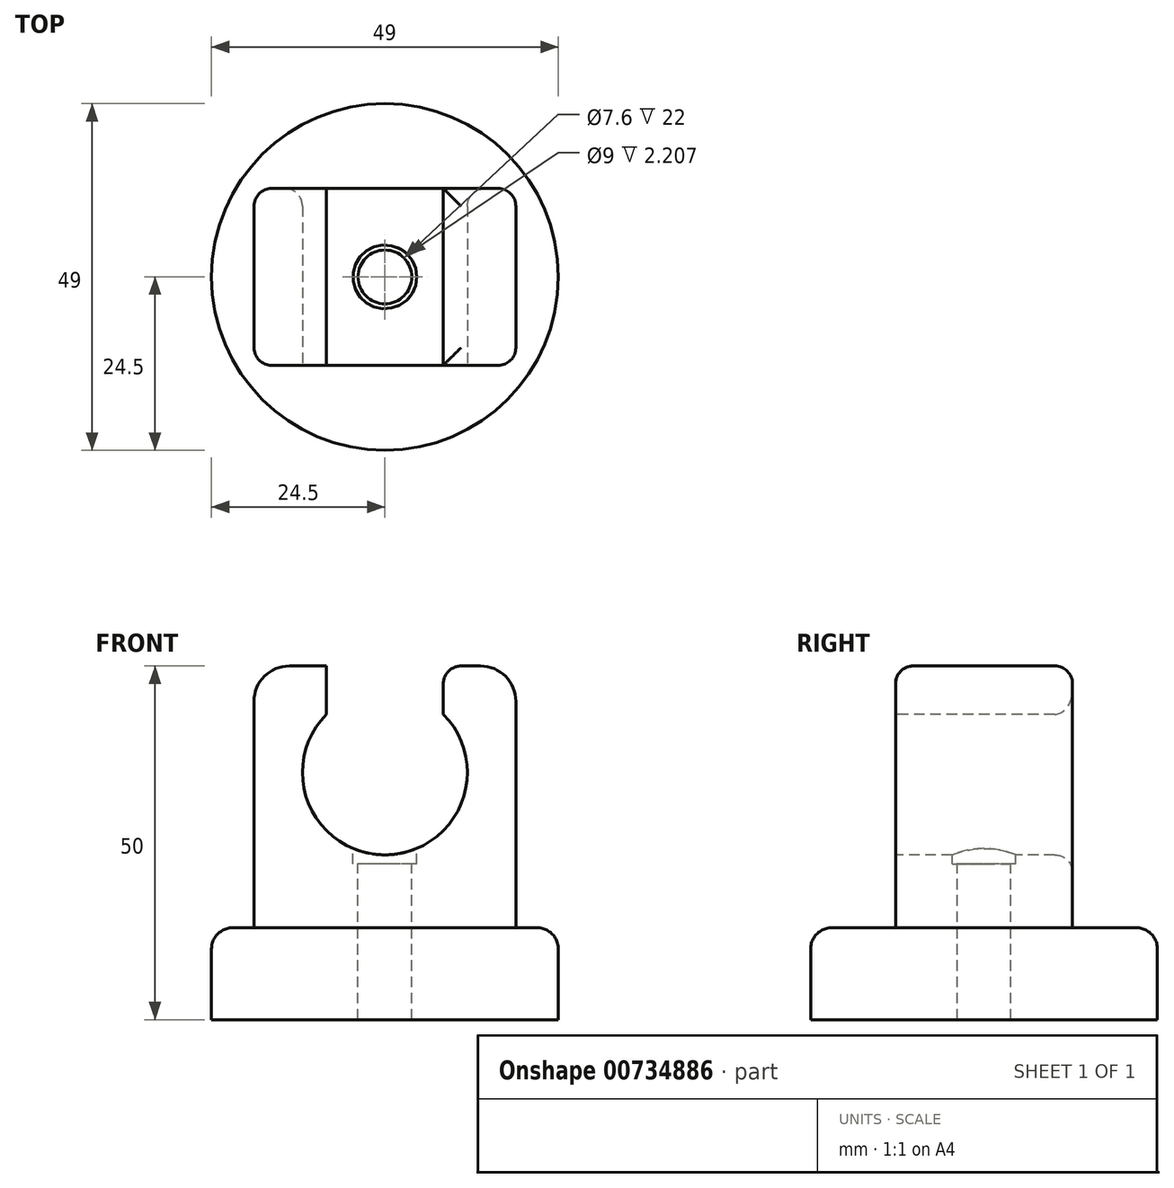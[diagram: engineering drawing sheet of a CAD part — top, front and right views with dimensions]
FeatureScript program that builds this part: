
annotation { "Feature Type Name" : "Feature", "Feature Type Description" : "" }
export const myFeature = defineFeature(function(context is Context, id is Id, definition is map)
    precondition{}
    {
        {
            var Q0;
            Q0=qCreatedBy(makeId("Top.planeOp"),FACE);
            var sketch = newSketch(context, id + "F0", { "sketchPlane" : qUnion([Q0])});
            skCircle(sketch, "E0", {"center": v(0, 0) * mm, "radius": 24.5 * mm});
            skSolve(sketch);
        }
        {
            var Q0;
            Q0=makeQuery(id+"F0.imprint","IMPRINT",FACE,{"disambiguationData":[TD([[makeQuery(id+"F0.imprint","IMPRINT",EDGE,{"derivedFrom":sQuery(id+"F0.wireOp",EDGE,"E0")}),1.0]])]});
            extrude(context, id + "F1", {"entities" : qUnion([Q0]), "depth" : 13 * mm, "offsetDistance" : 25.4 * mm});
        }
        {
            var Q0;
            Q0=makeQuery(id+"F1.opExtrude","CAP_FACE",FACE,{"disambiguationData":[OSD([sQuery(id+"F0.wireOp",EDGE,"E0")])],"isStart":false});
            var sketch = newSketch(context, id + "F2", { "sketchPlane" : qUnion([Q0])});
            skLineSegment(sketch, "E1.bottom", {"start": v(18.5, 12.5) * mm, "end": v(-18.5, 12.5) * mm});
            skLineSegment(sketch, "E1.top", {"start": v(18.5, -12.5) * mm, "end": v(-18.5, -12.5) * mm});
            skLineSegment(sketch, "E1.left", {"start": v(18.5, 12.5) * mm, "end": v(18.5, -12.5) * mm});
            skLineSegment(sketch, "E1.right", {"start": v(-18.5, 12.5) * mm, "end": v(-18.5, -12.5) * mm});
            skPoint(sketch, "E1.middle", {"position": v(0, 0) * mm});
            skSolve(sketch);
        }
        {
            var Q0;
            Q0=makeQuery(id+"F2.imprint","IMPRINT",FACE,{"disambiguationData":[TD([[makeQuery(id+"F2.imprint","IMPRINT",EDGE,{"derivedFrom":sQuery(id+"F2.wireOp",EDGE,"E1.bottom")}),1.0]])]});
            extrude(context, id + "F3", {"entities" : qUnion([Q0]), "operationType" : NewBodyOperationType.ADD, "depth" : 37 * mm, "offsetDistance" : 25.4 * mm});
        }
        {
            var Q0;
            Q0=makeQuery(id+"F1.opExtrude","CAP_EDGE",EDGE,{"disambiguationData":[OSD([sQuery(id+"F0.wireOp",EDGE,"E0")])],"isStart":false});
            fillet(context, id + "F4", {"entities" : qUnion([Q0]), "radius" : 3 * mm, "tangentPropagation" : true, "allowEdgeOverflow" : false});
        }
        {
            var Q0;
            Q0=makeQuery(id+"F3.opExtrude","CAP_FACE",FACE,{"disambiguationData":[OSD([sQuery(id+"F2.wireOp",EDGE,"E1.bottom"),sQuery(id+"F2.wireOp",EDGE,"E1.top"),sQuery(id+"F2.wireOp",EDGE,"E1.left"),sQuery(id+"F2.wireOp",EDGE,"E1.right")])],"isStart":false});
            var sketch = newSketch(context, id + "F5", { "sketchPlane" : qUnion([Q0])});
            skCircle(sketch, "E2", {"center": v(0, 0) * mm, "radius": 3.8 * mm});
            skSolve(sketch);
        }
        {
            var Q0;
            Q0=makeQuery(id+"F5.imprint","IMPRINT",FACE,{"disambiguationData":[TD([[makeQuery(id+"F5.imprint","IMPRINT",EDGE,{"derivedFrom":sQuery(id+"F5.wireOp",EDGE,"E2")}),1.0]])]});
            extrude(context, id + "F6", {"entities" : qUnion([Q0]), "operationType" : NewBodyOperationType.REMOVE, "oppositeDirection" : true, "depth" : 60 * mm, "offsetDistance" : 25.4 * mm});
        }
        {
            var Q0;
            Q0=makeQuery(id+"F3.opExtrude","SWEPT_FACE",FACE,{"disambiguationData":[OSD([sQuery(id+"F2.wireOp",EDGE,"E1.top")])]});
            var sketch = newSketch(context, id + "F7", { "sketchPlane" : qUnion([Q0])});
            skCircle(sketch, "E3", {"center": v(0, 34.95) * mm, "radius": 11.65 * mm});
            skSolve(sketch);
        }
        {
            var Q0;
            Q0=makeQuery(id+"F7.imprint","IMPRINT",FACE,{"disambiguationData":[TD([[makeQuery(id+"F7.imprint","IMPRINT",EDGE,{"derivedFrom":sQuery(id+"F7.wireOp",EDGE,"E3")}),1.0]])]});
            extrude(context, id + "F8", {"entities" : qUnion([Q0]), "operationType" : NewBodyOperationType.REMOVE, "oppositeDirection" : true, "depth" : 40 * mm, "offsetDistance" : 25.4 * mm});
        }
        {
            var Q0;
            Q0=makeQuery(id+"F3.opExtrude","CAP_FACE",FACE,{"disambiguationData":[OSD([sQuery(id+"F2.wireOp",EDGE,"E1.bottom"),sQuery(id+"F2.wireOp",EDGE,"E1.top"),sQuery(id+"F2.wireOp",EDGE,"E1.left"),sQuery(id+"F2.wireOp",EDGE,"E1.right")])],"isStart":false});
            var sketch = newSketch(context, id + "F9", { "sketchPlane" : qUnion([Q0])});
            skLineSegment(sketch, "E4.bottom", {"start": v(8.25, 12.5) * mm, "end": v(-8.25, 12.5) * mm});
            skLineSegment(sketch, "E4.top", {"start": v(8.25, -12.5) * mm, "end": v(-8.25, -12.5) * mm});
            skLineSegment(sketch, "E4.left", {"start": v(8.25, 12.5) * mm, "end": v(8.25, -12.5) * mm});
            skLineSegment(sketch, "E4.right", {"start": v(-8.25, 12.5) * mm, "end": v(-8.25, -12.5) * mm});
            skPoint(sketch, "E4.middle", {"position": v(0, 0) * mm});
            skSolve(sketch);
        }
        {
            var Q0;
            Q0 = qSketchRegion(id + "F9", true);
            extrude(context, id + "F10", {"entities" : qUnion([Q0]), "operationType" : NewBodyOperationType.REMOVE, "oppositeDirection" : true, "depth" : 10 * mm, "offsetDistance" : 25.4 * mm});
        }
        {
            var Q0;
            {var subQ0=sQuery(id+"F2.wireOp",EDGE,"E1.bottom");var subQ1=sQuery(id+"F2.wireOp",EDGE,"E1.right");var subQ2=sQuery(id+"F2.wireOp",EDGE,"E1.top");Q0=makeQuery(id+"F10.boolean.opBoolean","SPLIT",FACE,{"disambiguationData":[TD([makeQuery(id+"F3.opExtrude","SWEPT_FACE",FACE,{"disambiguationData":[OSD([subQ1])]})])],"derivedFrom":makeQuery(id+"F3.opExtrude","CAP_FACE",FACE,{"disambiguationData":[OSD([subQ0,subQ2,sQuery(id+"F2.wireOp",EDGE,"E1.left"),subQ1])],"isStart":false})});}
            var sketch = newSketch(context, id + "F11", { "sketchPlane" : qUnion([Q0])});
            skCircle(sketch, "E5", {"center": v(0, 0) * mm, "radius": 4.5 * mm});
            skSolve(sketch);
        }
        {
            var Q0;
            Q0 = qSketchRegion(id + "F11", true);
            extrude(context, id + "F12", {"entities" : qUnion([Q0]), "operationType" : NewBodyOperationType.REMOVE, "oppositeDirection" : true, "depth" : 28 * mm, "offsetDistance" : 25.4 * mm});
        }
        {
            var Q0;
            Q0=makeQuery(id+"F3.opExtrude","SWEPT_EDGE",EDGE,{"disambiguationData":[OSD([sQuery(id+"F2.wireOp",EDGE,"E1.bottom"),sQuery(id+"F2.wireOp",EDGE,"E1.left")])]});
            var Q1;
            Q1=makeQuery(id+"F3.opExtrude","SWEPT_EDGE",EDGE,{"disambiguationData":[OSD([sQuery(id+"F2.wireOp",EDGE,"E1.bottom"),sQuery(id+"F2.wireOp",EDGE,"E1.right")])]});
            var Q2;
            Q2=makeQuery(id+"F3.opExtrude","SWEPT_EDGE",EDGE,{"disambiguationData":[OSD([sQuery(id+"F2.wireOp",EDGE,"E1.top"),sQuery(id+"F2.wireOp",EDGE,"E1.left")])]});
            var Q3;
            Q3=makeQuery(id+"F3.opExtrude","SWEPT_EDGE",EDGE,{"disambiguationData":[OSD([sQuery(id+"F2.wireOp",EDGE,"E1.top"),sQuery(id+"F2.wireOp",EDGE,"E1.right")])]});
            var Q4;
            {var subQ0=sQuery(id+"F2.wireOp",EDGE,"E1.right");var subQ1=sQuery(id+"F2.wireOp",EDGE,"E1.top");Q4=makeQuery(id+"F10.boolean.opBoolean","SPLIT",EDGE,{"disambiguationData":[TD([makeQuery(id+"F3.opExtrude","SWEPT_FACE",FACE,{"disambiguationData":[OSD([subQ0])]})])],"derivedFrom":makeQuery(id+"F3.opExtrude","CAP_EDGE",EDGE,{"disambiguationData":[OSD([subQ1])],"isStart":false})});}
            var Q5;
            {var subQ0=sQuery(id+"F2.wireOp",EDGE,"E1.left");var subQ1=sQuery(id+"F2.wireOp",EDGE,"E1.top");Q5=makeQuery(id+"F10.boolean.opBoolean","SPLIT",EDGE,{"disambiguationData":[TD([makeQuery(id+"F3.opExtrude","SWEPT_FACE",FACE,{"disambiguationData":[OSD([subQ0])]})])],"derivedFrom":makeQuery(id+"F3.opExtrude","CAP_EDGE",EDGE,{"disambiguationData":[OSD([subQ1])],"isStart":false})});}
            var Q6;
            {var subQ0=sQuery(id+"F2.wireOp",EDGE,"E1.bottom");var subQ1=sQuery(id+"F2.wireOp",EDGE,"E1.right");Q6=makeQuery(id+"F10.boolean.opBoolean","SPLIT",EDGE,{"disambiguationData":[TD([makeQuery(id+"F3.opExtrude","SWEPT_FACE",FACE,{"disambiguationData":[OSD([subQ1])]})])],"derivedFrom":makeQuery(id+"F3.opExtrude","CAP_EDGE",EDGE,{"disambiguationData":[OSD([subQ0])],"isStart":false})});}
            var Q7;
            {var subQ0=sQuery(id+"F2.wireOp",EDGE,"E1.bottom");var subQ1=sQuery(id+"F2.wireOp",EDGE,"E1.left");Q7=makeQuery(id+"F10.boolean.opBoolean","SPLIT",EDGE,{"disambiguationData":[TD([makeQuery(id+"F3.opExtrude","SWEPT_FACE",FACE,{"disambiguationData":[OSD([subQ1])]})])],"derivedFrom":makeQuery(id+"F3.opExtrude","CAP_EDGE",EDGE,{"disambiguationData":[OSD([subQ0])],"isStart":false})});}
            var Q8;
            Q8=makeQuery(id+"F10.boolean.opBoolean","COPY",EDGE,{"derivedFrom":makeQuery(id+"F10.opExtrude","SWEPT_EDGE",EDGE,{"disambiguationData":[OSD([sQuery(id+"F2.wireOp",EDGE,"E1.top"),sQuery(id+"F9.wireOp",EDGE,"E4.top"),sQuery(id+"F9.wireOp",EDGE,"E4.right")])]})});
            var Q9;
            Q9=makeQuery(id+"F10.boolean.opBoolean","COPY",EDGE,{"derivedFrom":makeQuery(id+"F10.opExtrude","SWEPT_EDGE",EDGE,{"disambiguationData":[OSD([sQuery(id+"F2.wireOp",EDGE,"E1.top"),sQuery(id+"F9.wireOp",EDGE,"E4.top"),sQuery(id+"F9.wireOp",EDGE,"E4.left")])]})});
            var Q10;
            Q10=makeQuery(id+"F10.boolean.opBoolean","COPY",EDGE,{"derivedFrom":makeQuery(id+"F10.opExtrude","SWEPT_EDGE",EDGE,{"disambiguationData":[OSD([sQuery(id+"F2.wireOp",EDGE,"E1.bottom"),sQuery(id+"F9.wireOp",EDGE,"E4.bottom"),sQuery(id+"F9.wireOp",EDGE,"E4.left")])]})});
            var Q11;
            Q11=makeQuery(id+"F10.boolean.opBoolean","COPY",EDGE,{"derivedFrom":makeQuery(id+"F10.opExtrude","SWEPT_EDGE",EDGE,{"disambiguationData":[OSD([sQuery(id+"F2.wireOp",EDGE,"E1.bottom"),sQuery(id+"F9.wireOp",EDGE,"E4.bottom"),sQuery(id+"F9.wireOp",EDGE,"E4.right")])]})});
            var Q12;
            Q12=makeQuery(id+"F10.boolean.opBoolean","COPY",EDGE,{"derivedFrom":makeQuery(id+"F10.opExtrude","CAP_EDGE",EDGE,{"disambiguationData":[OSD([sQuery(id+"F9.wireOp",EDGE,"E4.left")])],"isStart":true})});
            var Q13;
            Q13=makeQuery(id+"F10.boolean.opBoolean","COPY",EDGE,{"derivedFrom":makeQuery(id+"F10.opExtrude","CAP_EDGE",EDGE,{"disambiguationData":[OSD([sQuery(id+"F9.wireOp",EDGE,"E4.right")])],"isStart":true})});
            var Q14;
            Q14=makeQuery(id+"F8.boolean.opBoolean","INTERSECT",EDGE,{"derivedFrom":[makeQuery(id+"F3.opExtrude","SWEPT_FACE",FACE,{"disambiguationData":[OSD([sQuery(id+"F2.wireOp",EDGE,"E1.bottom")])]}),makeQuery(id+"F8.opExtrude","SWEPT_FACE",FACE,{"disambiguationData":[OSD([sQuery(id+"F7.wireOp",EDGE,"E3")])]})]});
            var Q15;
            Q15=makeQuery(id+"F8.boolean.opBoolean","COPY",EDGE,{"derivedFrom":makeQuery(id+"F8.opExtrude","CAP_EDGE",EDGE,{"disambiguationData":[OSD([sQuery(id+"F7.wireOp",EDGE,"E3")])],"isStart":true})});
            fillet(context, id + "F13", {"entities" : qUnion([Q0, Q1, Q2, Q3, Q4, Q5, Q6, Q7, Q8, Q9, Q10, Q11, Q12, Q13, Q14, Q15]), "radius" : 2.5 * mm, "tangentPropagation" : true, "allowEdgeOverflow" : false});
        }
        {
            var Q0;
            Q0=makeQuery(id+"F3.opExtrude","CAP_EDGE",EDGE,{"disambiguationData":[OSD([sQuery(id+"F2.wireOp",EDGE,"E1.left")])],"isStart":false});
            var Q1;
            Q1=makeQuery(id+"F3.opExtrude","CAP_EDGE",EDGE,{"disambiguationData":[OSD([sQuery(id+"F2.wireOp",EDGE,"E1.right")])],"isStart":false});
            fillet(context, id + "F14", {"entities" : qUnion([Q0, Q1]), "radius" : 5 * mm, "tangentPropagation" : true, "allowEdgeOverflow" : false});
        }
    });
